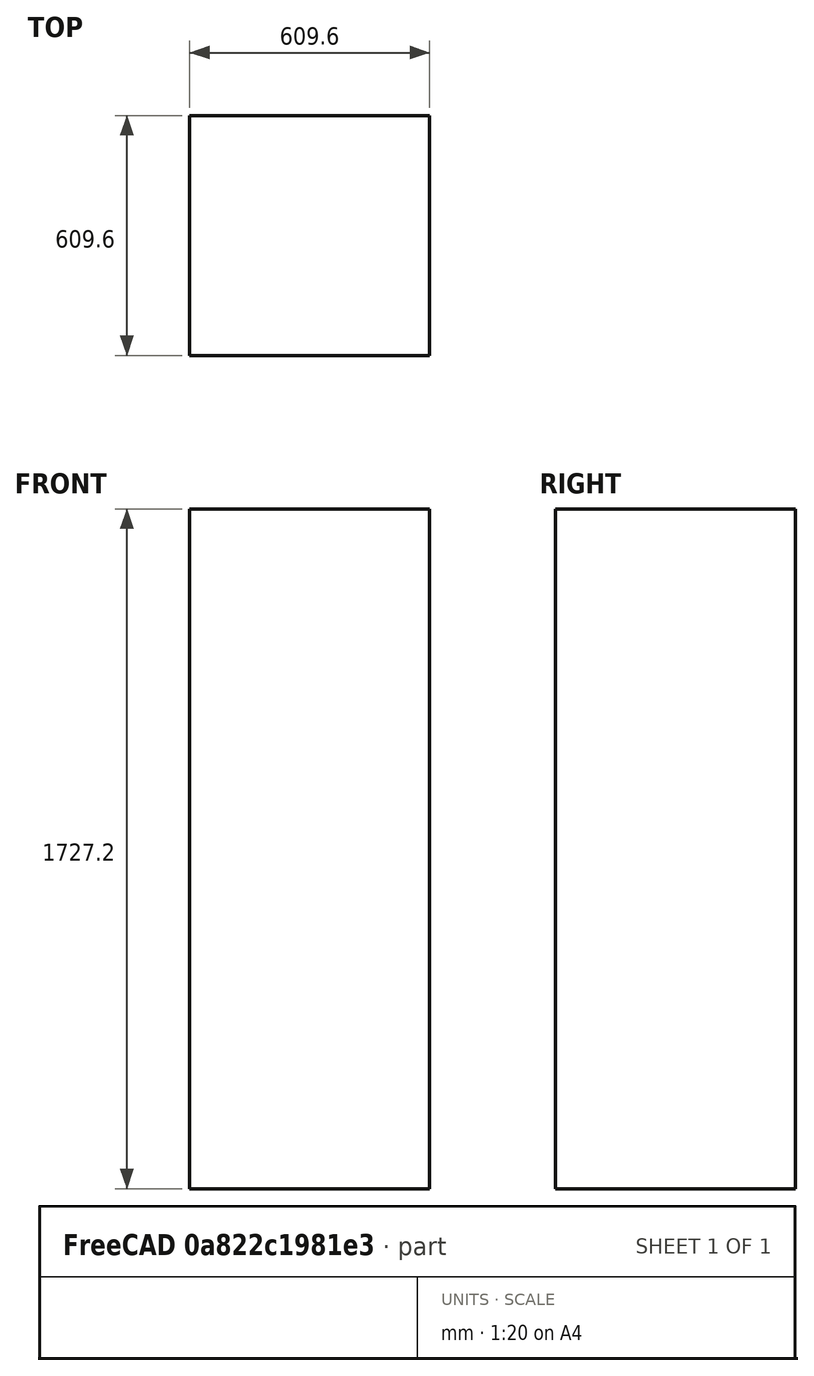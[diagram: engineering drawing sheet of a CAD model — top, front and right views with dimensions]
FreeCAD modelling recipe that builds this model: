
FCSTD DOCUMENT  (FreeCAD 2023.131R26244 +5365 (Git))
Label: human
License: All rights reserved
LicenseURL: http://en.wikipedia.org/wiki/All_rights_reserved
objects: Sketcher::SketchObject×1, PartDesign::Pad×1, PartDesign::Body×1, App::Part×1
note: 6 computed .brp shape members not serialized (recipe doc carries the construction recipe); baked Part::Feature solids carry a one-line shape summary decoded from their .brp

FEATURE [Sketcher::SketchObject] Sketch
  ArcFitTolerance = 1e-06
  AttachmentSupport = -> [XY_Plane]
  ExternalBSplineMaxDegree = 5
  ExternalBSplineTolerance = 0.0001
  FixShape = 1
  FullyConstrained = true
  InternalTolerance = 1e-06
  InvalidShape = false
  MakeInternals = false
  MapMode = 5
  Support = -> [XY_Plane]
  TreeRank = 13
  ValidateShape = false
  sketch-geometry (4):
    g0: LineSegment StartX=0 StartY=0 StartZ=0 EndX=609.6 EndY=0 EndZ=0
    g1: LineSegment StartX=609.6 StartY=0 StartZ=0 EndX=609.6 EndY=609.6 EndZ=0
    g2: LineSegment StartX=609.6 StartY=609.6 StartZ=0 EndX=0 EndY=609.6 EndZ=0
    g3: LineSegment StartX=0 StartY=609.6 StartZ=0 EndX=0 EndY=0 EndZ=0
  constraints (11):
    c: Coincident(g0,g1)
    c: Coincident(g1,g2)
    c: Coincident(g2,g3)
    c: Coincident(g3,g0)
    c: Horizontal(g0)
    c: Horizontal(g2)
    c: Vertical(g1)
    c: Vertical(g3)
    c: Coincident(g0,g-1)
    c: DistanceX(g0,g0) = 609.6
    c: DistanceY(g3,g3) = 609.6
FEATURE [PartDesign::Pad] Pad
  AddSubType = 0
  AlongSketchNormal = false
  AutoTaperInnerAngle = true
  CheckUpToFaceLimits = true
  ClaimChildren = false
  Direction = (0,0,1)
  Fit = 0
  FitJoin = 0
  FixShape = 1
  InnerFit = 0
  InnerFitJoin = 0
  InvalidShape = false
  Length = 1727.2
  Length2 = 100
  Linearize = true
  NewSolid = false
  Profile = -> Sketch
  Suppress = false
  TaperInnerAngle = 0
  TaperInnerAngleRev = 0
  TreeRank = 14
  Type = 0
  ValidateShape = false
  _ProfileBasedVersion = 1
FEATURE [PartDesign::Body] Body
  AutoGroupSolids = false
  ClaimAllChildren = false
  ExportMode = 0
  FixShape = 1
  Group = -> [Sketch,Pad]
  InvalidShape = false
  Origin = -> Origin001
  Tip = -> Pad
  TreeRank = 12
  ValidateShape = false
  _ExportChildren = -> [Pad]
  _GroupVersion = 1
FEATURE [App::Part] Part  label="human-Part"
  ClaimAllChildren = false
  ExportMode = 1
  Group = -> [Body]
  Origin = -> Origin
  TreeRank = 1
  _ExportChildren = -> [Body]
  _GroupVersion = 1
